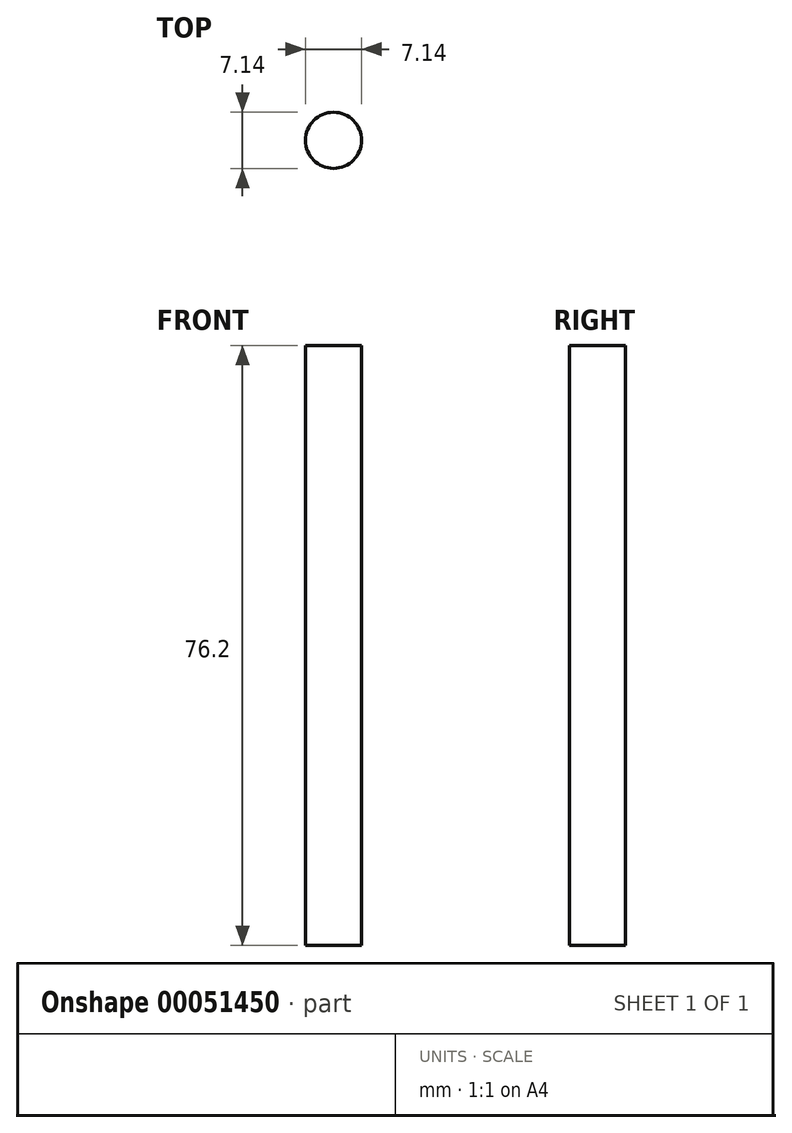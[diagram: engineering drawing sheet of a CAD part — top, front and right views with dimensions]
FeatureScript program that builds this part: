
annotation { "Feature Type Name" : "Feature", "Feature Type Description" : "" }
export const myFeature = defineFeature(function(context is Context, id is Id, definition is map)
    precondition{}
    {
        {
            var Q0;
            Q0=qCreatedBy(makeId("Front.planeOp"),FACE);
            var sketch = newSketch(context, id + "F0", { "sketchPlane" : qUnion([Q0])});
            skLineSegment(sketch, "E0.bottom", {"start": v(-61.44, 76.2) * mm, "end": v(33.8, 76.2) * mm});
            skLineSegment(sketch, "E0.top", {"start": v(-61.44, 0) * mm, "end": v(33.8, 0) * mm});
            skLineSegment(sketch, "E0.left", {"start": v(-61.44, 76.2) * mm, "end": v(-61.44, 0) * mm});
            skLineSegment(sketch, "E0.right", {"start": v(33.8, 76.2) * mm, "end": v(33.8, 0) * mm});
            skSolve(sketch);
        }
        {
            var Q0;
            Q0=makeQuery(id+"F0.imprint","IMPRINT",FACE,{"disambiguationData":[TD([[makeQuery(id+"F0.imprint","IMPRINT",EDGE,{"derivedFrom":sQuery(id+"F0.wireOp",EDGE,"E0.bottom")}),-1.0]])]});
            extrude(context, id + "F1", {"entities" : qUnion([Q0]), "depth" : 25.4 * mm});
        }
        {
            var Q0;
            Q0=makeQuery(id+"F1.opExtrude","CAP_FACE",FACE,{"disambiguationData":[OSD([sQuery(id+"F0.wireOp",EDGE,"E0.bottom"),sQuery(id+"F0.wireOp",EDGE,"E0.top"),sQuery(id+"F0.wireOp",EDGE,"E0.left"),sQuery(id+"F0.wireOp",EDGE,"E0.right")])],"isStart":false});
            var sketch = newSketch(context, id + "F2", { "sketchPlane" : qUnion([Q0])});
            skLineSegment(sketch, "E1.0", {"start": v(-13.94, 76.2) * mm, "end": v(-13.94, 0) * mm, "construction": true});
            skLineSegment(sketch, "E2", {"start": v(-61.44, 38.1) * mm, "end": v(33.8, 38.1) * mm, "construction": true});
            skCircle(sketch, "E3", {"center": v(-13.82, 38.1) * mm, "radius": 23.75 * mm});
            skSolve(sketch);
        }
        {
            var Q0;
            Q0=makeQuery(id+"F2.imprint","IMPRINT",FACE,{"disambiguationData":[TD([[makeQuery(id+"F2.imprint","IMPRINT",EDGE,{"derivedFrom":sQuery(id+"F2.wireOp",EDGE,"E3")}),1.0]])]});
            extrude(context, id + "F3", {"entities" : qUnion([Q0]), "operationType" : NewBodyOperationType.REMOVE, "oppositeDirection" : true, "depth" : 25.4 * mm});
        }
        {
            var Q0;
            Q0=makeQuery(id+"F1.opExtrude","SWEPT_FACE",FACE,{"disambiguationData":[OSD([sQuery(id+"F0.wireOp",EDGE,"E0.bottom")])]});
            var sketch = newSketch(context, id + "F4", { "sketchPlane" : qUnion([Q0])});
            skLineSegment(sketch, "E4", {"start": v(-61.44, -12.7) * mm, "end": v(33.8, -12.7) * mm, "construction": true});
            skLineSegment(sketch, "E5", {"start": v(-13.82, 0) * mm, "end": v(-13.82, -25.4) * mm, "construction": true});
            skLineSegment(sketch, "E6.0", {"start": v(24.28, -25.4) * mm, "end": v(24.28, 0) * mm, "construction": true});
            skCircle(sketch, "E7", {"center": v(24.28, -12.7) * mm, "radius": 3.57 * mm});
            skCircle(sketch, "E8.MirrorC", {"center": v(-51.92, -12.7) * mm, "radius": 3.57 * mm});
            skSolve(sketch);
        }
        {
            var Q0;
            Q0=makeQuery(id+"F4.imprint","IMPRINT",FACE,{"disambiguationData":[TD([[makeQuery(id+"F4.imprint","IMPRINT",EDGE,{"derivedFrom":sQuery(id+"F4.wireOp",EDGE,"E7")}),1.0]])]});
            var Q1;
            Q1=makeQuery(id+"F4.imprint","IMPRINT",FACE,{"disambiguationData":[TD([[makeQuery(id+"F4.imprint","IMPRINT",EDGE,{"derivedFrom":sQuery(id+"F4.wireOp",EDGE,"E8.MirrorC")}),-1.0]])]});
            extrude(context, id + "F5", {"entities" : qUnion([Q0, Q1]), "operationType" : NewBodyOperationType.REMOVE, "endBound" : BoundingType.THROUGH_ALL, "oppositeDirection" : true, "depth" : 25.4 * mm});
        }
    });
